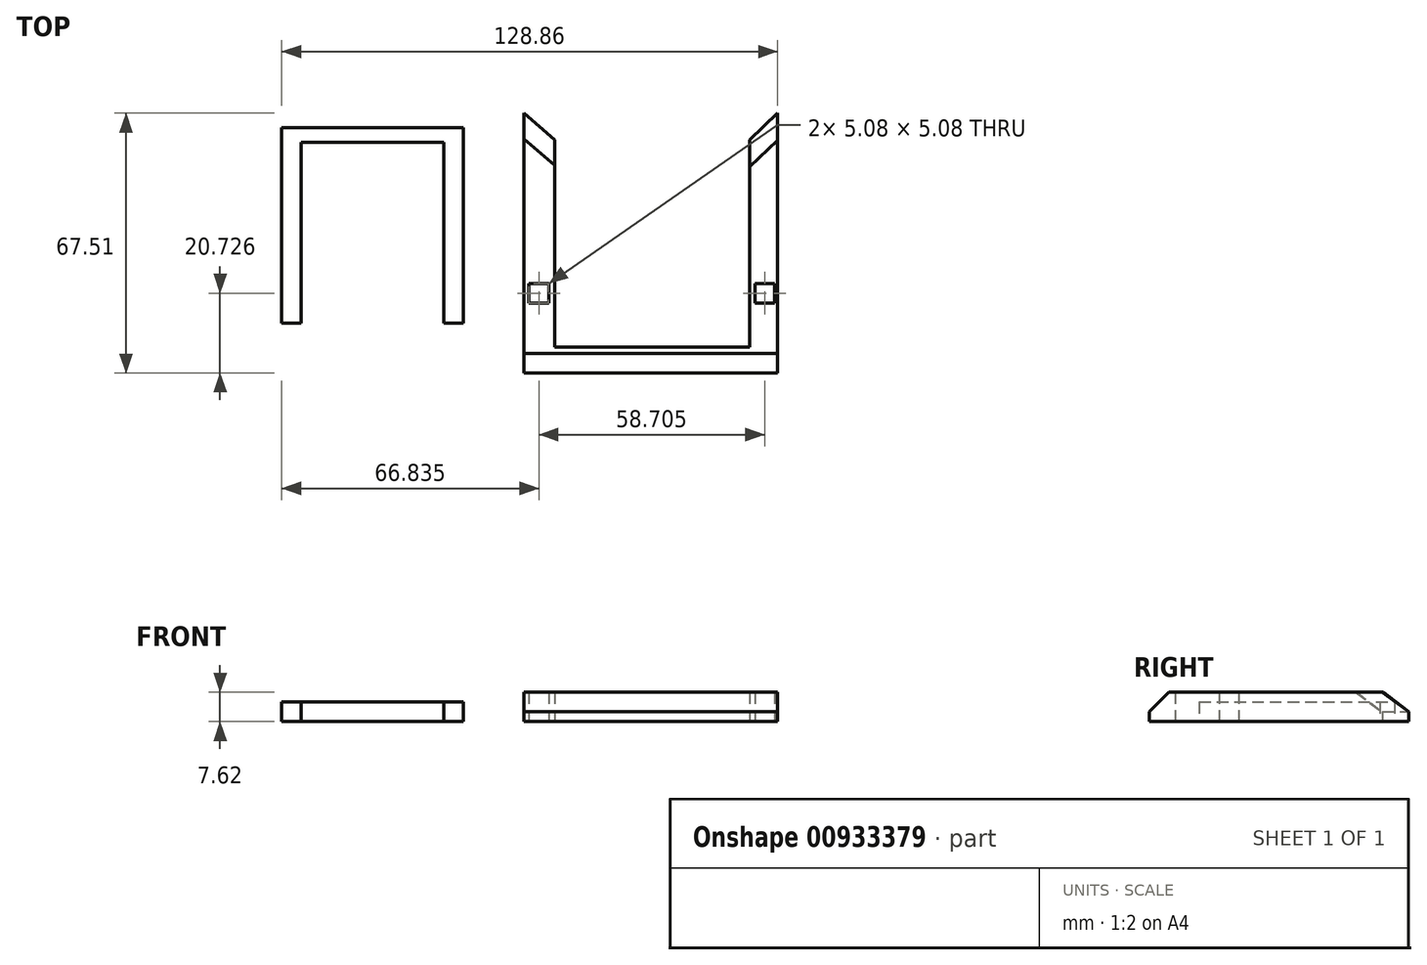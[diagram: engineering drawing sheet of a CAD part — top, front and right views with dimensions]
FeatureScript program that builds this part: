
annotation { "Feature Type Name" : "Feature", "Feature Type Description" : "" }
export const myFeature = defineFeature(function(context is Context, id is Id, definition is map)
    precondition{}
    {
        {
            var Q0;
            Q0=qCreatedBy(makeId("Top.planeOp"),FACE);
            var sketch = newSketch(context, id + "F0", { "sketchPlane" : qUnion([Q0])});
            skLineSegment(sketch, "E0.bottom", {"start": v(-57.97, -3.5) * mm, "end": v(-52.9, -3.5) * mm});
            skLineSegment(sketch, "E0.top", {"start": v(-57.97, 47.3) * mm, "end": v(-52.9, 47.3) * mm});
            skLineSegment(sketch, "E0.left", {"start": v(-57.97, -3.5) * mm, "end": v(-57.97, 47.3) * mm});
            skLineSegment(sketch, "E0.right", {"start": v(-52.9, -3.5) * mm, "end": v(-52.9, 47.3) * mm});
            skLineSegment(sketch, "E1.bottom", {"start": v(-15.8, -3.5) * mm, "end": v(-10.71, -3.5) * mm});
            skLineSegment(sketch, "E1.top", {"start": v(-15.8, 47.3) * mm, "end": v(-10.71, 47.3) * mm});
            skLineSegment(sketch, "E1.left", {"start": v(-15.8, -3.5) * mm, "end": v(-15.8, 47.3) * mm});
            skLineSegment(sketch, "E1.right", {"start": v(-10.71, -3.5) * mm, "end": v(-10.71, 47.3) * mm});
            skLineSegment(sketch, "E2.bottom", {"start": v(-52.9, 47.3) * mm, "end": v(-15.8, 47.3) * mm});
            skLineSegment(sketch, "E2.top", {"start": v(-52.9, 43.5) * mm, "end": v(-15.8, 43.5) * mm});
            skLineSegment(sketch, "E2.left", {"start": v(-52.9, 47.3) * mm, "end": v(-52.9, 43.5) * mm});
            skLineSegment(sketch, "E2.right", {"start": v(-15.8, 47.3) * mm, "end": v(-15.8, 43.5) * mm});
            skSolve(sketch);
        }
        {
            var Q0;
            {var subQ0=sQuery(id+"F0.wireOp",EDGE,"E2.bottom");var subQ10=sQuery(id+"F0.wireOp",EDGE,"E1.bottom");var subQ11=sQuery(id+"F0.wireOp",EDGE,"E0.bottom");Q0=qUnion([makeQuery(id+"F0.imprint","IMPRINT",FACE,{"disambiguationData":[TD([[makeQuery(id+"F0.imprint","IMPRINT",EDGE,{"derivedFrom":subQ11}),1.0]])]}),makeQuery(id+"F0.imprint","IMPRINT",FACE,{"disambiguationData":[TD([[makeQuery(id+"F0.imprint","IMPRINT",EDGE,{"derivedFrom":subQ10}),1.0]])]}),makeQuery(id+"F0.imprint","IMPRINT",FACE,{"disambiguationData":[TD([[makeQuery(id+"F0.imprint","IMPRINT",EDGE,{"derivedFrom":subQ0}),-1.0]])]})]);}
            extrude(context, id + "F1", {"entities" : qUnion([Q0]), "depth" : 5.08 * mm, "offsetDistance" : 25.4 * mm});
        }
        {
            var Q0;
            Q0=qCreatedBy(makeId("Top.planeOp"),FACE);
            var sketch = newSketch(context, id + "F2", { "sketchPlane" : qUnion([Q0])});
            skLineSegment(sketch, "E3.bottom", {"start": v(5.01, 51.04) * mm, "end": v(70.9, 51.04) * mm});
            skLineSegment(sketch, "E3.top", {"start": v(5.01, -16.47) * mm, "end": v(70.9, -16.47) * mm});
            skLineSegment(sketch, "E3.left", {"start": v(5.01, 51.04) * mm, "end": v(5.01, -16.47) * mm});
            skLineSegment(sketch, "E3.right", {"start": v(70.9, 51.04) * mm, "end": v(70.9, -16.47) * mm});
            skLineSegment(sketch, "E4.bottom", {"start": v(13.04, 44.16) * mm, "end": v(63.68, 44.16) * mm});
            skLineSegment(sketch, "E4.top", {"start": v(13.04, -9.75) * mm, "end": v(63.68, -9.75) * mm});
            skLineSegment(sketch, "E4.left", {"start": v(13.04, 44.16) * mm, "end": v(13.04, -9.75) * mm});
            skLineSegment(sketch, "E4.right", {"start": v(63.68, 44.16) * mm, "end": v(63.68, -9.75) * mm});
            skLineSegment(sketch, "E5.bottom", {"start": v(6.33, 6.8) * mm, "end": v(11.4, 6.8) * mm});
            skLineSegment(sketch, "E5.top", {"start": v(6.33, 1.72) * mm, "end": v(11.4, 1.72) * mm});
            skLineSegment(sketch, "E5.left", {"start": v(6.33, 6.8) * mm, "end": v(6.33, 1.72) * mm});
            skLineSegment(sketch, "E5.right", {"start": v(11.4, 6.8) * mm, "end": v(11.4, 1.72) * mm});
            skLineSegment(sketch, "E6", {"start": v(11.4, 1.72) * mm, "end": v(70.9, 1.72) * mm});
            skLineSegment(sketch, "E7.bottom", {"start": v(70.11, 1.72) * mm, "end": v(65.03, 1.72) * mm});
            skLineSegment(sketch, "E7.top", {"start": v(70.11, 6.8) * mm, "end": v(65.03, 6.8) * mm});
            skLineSegment(sketch, "E7.left", {"start": v(70.11, 1.72) * mm, "end": v(70.11, 6.8) * mm});
            skLineSegment(sketch, "E7.right", {"start": v(65.03, 1.72) * mm, "end": v(65.03, 6.8) * mm});
            skLineSegment(sketch, "E8", {"start": v(5.01, 51.04) * mm, "end": v(13.04, 44.16) * mm});
            skLineSegment(sketch, "E9", {"start": v(70.9, 51.04) * mm, "end": v(63.68, 44.16) * mm});
            skSolve(sketch);
        }
        {
            var Q0;
            Q0=makeQuery(id+"F2.imprint","IMPRINT",FACE,{"disambiguationData":[TD([[makeQuery(id+"F2.imprint","IMPRINT",EDGE,{"derivedFrom":sQuery(id+"F2.wireOp",EDGE,"E7.top")}),-1.0]])]});
            var Q1;
            {var subQ7=sQuery(id+"F2.wireOp",EDGE,"E3.top");Q1=makeQuery(id+"F2.imprint","IMPRINT",FACE,{"disambiguationData":[TD([[makeQuery(id+"F2.imprint","IMPRINT",EDGE,{"derivedFrom":subQ7}),1.0]])]});}
            extrude(context, id + "F3", {"entities" : qUnion([Q0, Q1]), "depth" : 7.62 * mm, "offsetDistance" : 25.4 * mm});
        }
        {
            var Q0;
            Q0=makeQuery(id+"F3.opExtrude","CAP_EDGE",EDGE,{"disambiguationData":[OSD([sQuery(id+"F2.wireOp",EDGE,"E3.top")])],"isStart":false});
            var Q1;
            Q1=makeQuery(id+"F3.opExtrude","CAP_EDGE",EDGE,{"disambiguationData":[OSD([sQuery(id+"F2.wireOp",EDGE,"E8")])],"isStart":false});
            var Q2;
            Q2=makeQuery(id+"F3.opExtrude","CAP_EDGE",EDGE,{"disambiguationData":[OSD([sQuery(id+"F2.wireOp",EDGE,"E9")])],"isStart":false});
            chamfer(context, id + "F4", {"entities" : qUnion([Q0, Q1, Q2]), "width" : 5.08 * mm, "tangentPropagation" : true});
        }
    });
